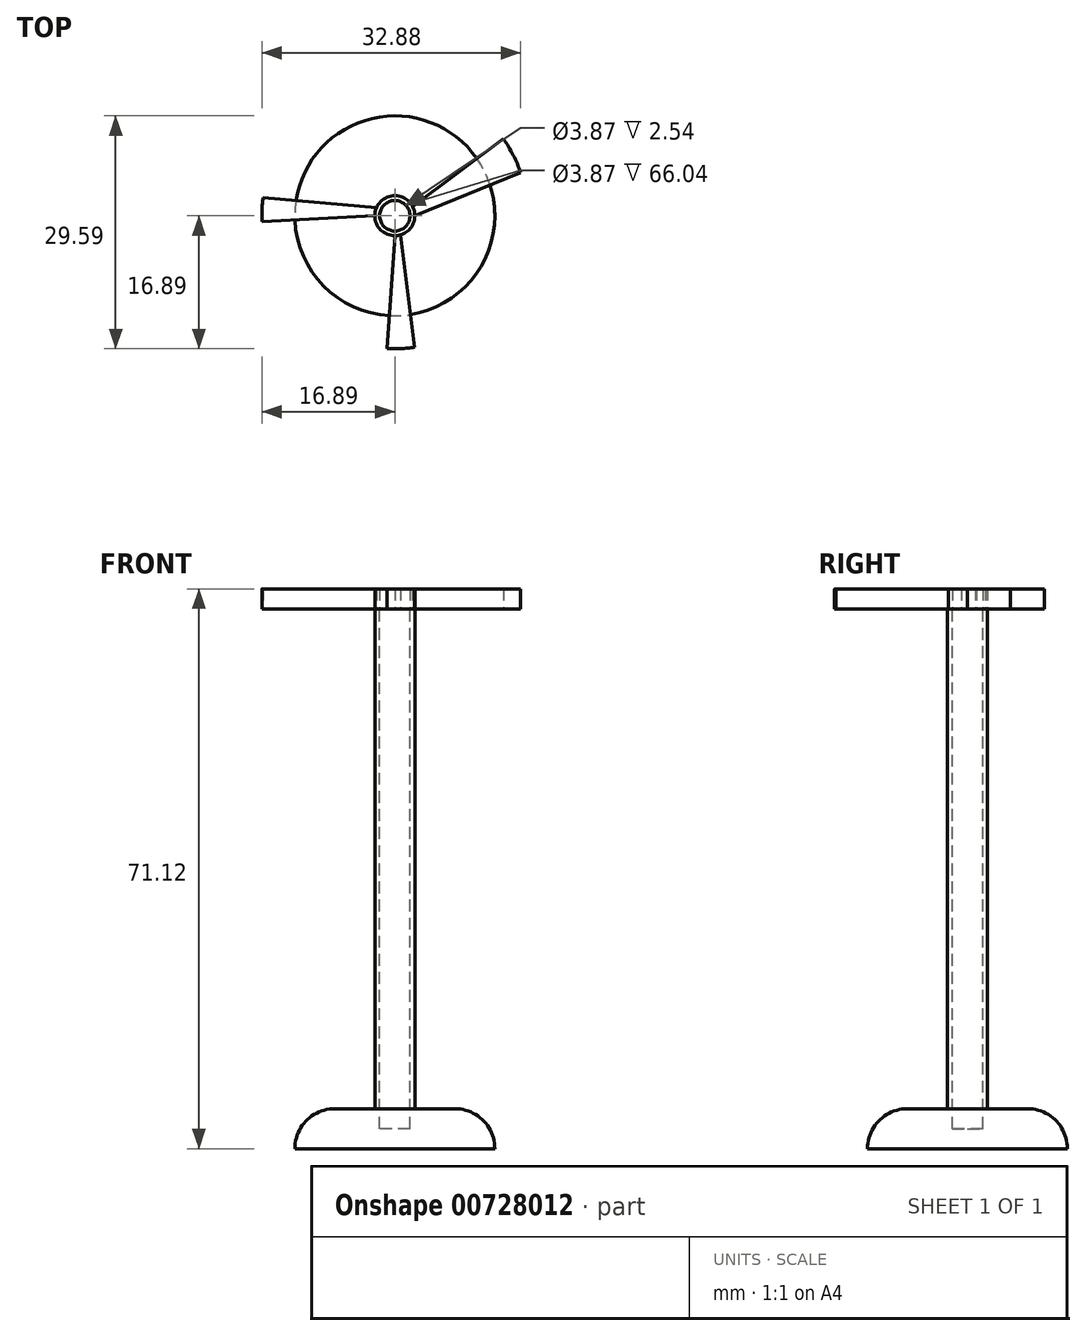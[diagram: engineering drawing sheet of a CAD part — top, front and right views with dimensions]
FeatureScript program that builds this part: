
annotation { "Feature Type Name" : "Feature", "Feature Type Description" : "" }
export const myFeature = defineFeature(function(context is Context, id is Id, definition is map)
    precondition{}
    {
        {
            var Q0;
            Q0=qCreatedBy(makeId("Top.planeOp"),FACE);
            var sketch = newSketch(context, id + "F0", { "sketchPlane" : qUnion([Q0])});
            skCircle(sketch, "E0", {"center": v(0, 0) * mm, "radius": 12.7 * mm});
            skSolve(sketch);
        }
        {
            var Q0;
            Q0=makeQuery(id+"F0.imprint","IMPRINT",FACE,{"disambiguationData":[TD([[makeQuery(id+"F0.imprint","IMPRINT",EDGE,{"derivedFrom":sQuery(id+"F0.wireOp",EDGE,"E0")}),1.0]])]});
            extrude(context, id + "F1", {"entities" : qUnion([Q0]), "depth" : 5.08 * mm, "offsetDistance" : 25.4 * mm});
        }
        {
            var Q0;
            Q0=makeQuery(id+"F1.opExtrude","CAP_FACE",FACE,{"disambiguationData":[OSD([sQuery(id+"F0.wireOp",EDGE,"E0")])],"isStart":false});
            var sketch = newSketch(context, id + "F2", { "sketchPlane" : qUnion([Q0])});
            skCircle(sketch, "E1", {"center": v(0, 0) * mm, "radius": 2.54 * mm});
            skSolve(sketch);
        }
        {
            var Q0;
            Q0=makeQuery(id+"F2.imprint","IMPRINT",FACE,{"disambiguationData":[TD([[makeQuery(id+"F2.imprint","IMPRINT",EDGE,{"derivedFrom":sQuery(id+"F2.wireOp",EDGE,"E1")}),1.0]])]});
            extrude(context, id + "F3", {"entities" : qUnion([Q0]), "operationType" : NewBodyOperationType.ADD, "depth" : 63.5 * mm, "offsetDistance" : 25.4 * mm});
        }
        {
            var Q0;
            Q0=makeQuery(id+"F3.opExtrude","CAP_FACE",FACE,{"disambiguationData":[OSD([sQuery(id+"F2.wireOp",EDGE,"E1")])],"isStart":false});
            var sketch = newSketch(context, id + "F4", { "sketchPlane" : qUnion([Q0])});
            skCircle(sketch, "E2", {"center": v(0, 0) * mm, "radius": 16.9 * mm});
            skCircle(sketch, "E3", {"center": v(0, 0) * mm, "radius": 1.93 * mm});
            skLineSegment(sketch, "E4", {"start": v(-16.74, 2.28) * mm, "end": v(-2.33, 1.01) * mm});
            skLineSegment(sketch, "E5", {"start": v(-16.88, -0.75) * mm, "end": v(-2.33, 0) * mm});
            skLineSegment(sketch, "E6", {"start": v(2.27, 1.14) * mm, "end": v(13.77, 9.78) * mm});
            skLineSegment(sketch, "E7", {"start": v(2.54, 0) * mm, "end": v(15.99, 5.46) * mm});
            skPoint(sketch, "E7.endSnap0", {"position": v(8.02, 5.46) * mm});
            skLineSegment(sketch, "E8", {"start": v(0, -2.54) * mm, "end": v(-1, -16.86) * mm});
            skLineSegment(sketch, "E9", {"start": v(0.75, -2.43) * mm, "end": v(2.5, -16.7) * mm});
            skSolve(sketch);
        }
        {
            var Q0;
            Q0=makeQuery(id+"F4.imprint","IMPRINT",FACE,{"disambiguationData":[TD([[makeQuery(id+"F4.imprint","IMPRINT",EDGE,{"derivedFrom":sQuery(id+"F4.wireOp",EDGE,"E3")}),1.0]])]});
            extrude(context, id + "F5", {"entities" : qUnion([Q0]), "operationType" : NewBodyOperationType.REMOVE, "oppositeDirection" : true, "depth" : 66.04 * mm, "offsetDistance" : 25.4 * mm});
        }
        {
            var Q0;
            Q0=sQuery(id+"F4.wireOp",EDGE,"E2");
            extrude(context, id + "F6", {"bodyType" : ToolBodyType.SURFACE, "surfaceEntities" : qUnion([Q0]), "depth" : 25.4 * mm, "offsetDistance" : 25.4 * mm});
        }
        {
            var Q0;
            Q0=makeQuery(id+"F1.opExtrude","CAP_EDGE",EDGE,{"disambiguationData":[OSD([sQuery(id+"F0.wireOp",EDGE,"E0")])],"isStart":false});
            fillet(context, id + "F7", {"entities" : qUnion([Q0]), "radius" : 5.08 * mm, "tangentPropagation" : true, "allowEdgeOverflow" : false});
        }
        {
            var Q0;
            {var subQ0=sQuery(id+"F4.wireOp",EDGE,"E4");Q0=makeQuery(id+"F4.imprint","IMPRINT",FACE,{"disambiguationData":[TD([[makeQuery(id+"F4.imprint","IMPRINT",EDGE,{"derivedFrom":subQ0}),-1.0]])]});}
            extrude(context, id + "F8", {"entities" : qUnion([Q0]), "depth" : 2.54 * mm, "offsetDistance" : 25.4 * mm});
        }
        {
            var Q0;
            {var subQ0=sQuery(id+"F4.wireOp",EDGE,"E6");Q0=makeQuery(id+"F4.imprint","IMPRINT",FACE,{"disambiguationData":[TD([[makeQuery(id+"F4.imprint","IMPRINT",EDGE,{"derivedFrom":subQ0}),-1.0]])]});}
            var Q1;
            {var subQ0=sQuery(id+"F4.wireOp",EDGE,"E8");Q1=makeQuery(id+"F4.imprint","IMPRINT",FACE,{"disambiguationData":[TD([[makeQuery(id+"F4.imprint","IMPRINT",EDGE,{"derivedFrom":subQ0}),1.0]])]});}
            extrude(context, id + "F9", {"entities" : qUnion([Q0, Q1]), "depth" : 2.54 * mm, "offsetDistance" : 25.4 * mm});
        }
        {
            var Q0;
            Q0=makeQuery(id+"F4.imprint","IMPRINT",FACE,{"disambiguationData":[TD([[makeQuery(id+"F4.imprint","IMPRINT",EDGE,{"derivedFrom":sQuery(id+"F4.wireOp",EDGE,"E3")}),-1.0]])]});
            extrude(context, id + "F10", {"entities" : qUnion([Q0]), "depth" : 2.54 * mm, "offsetDistance" : 25.4 * mm});
        }
    });
